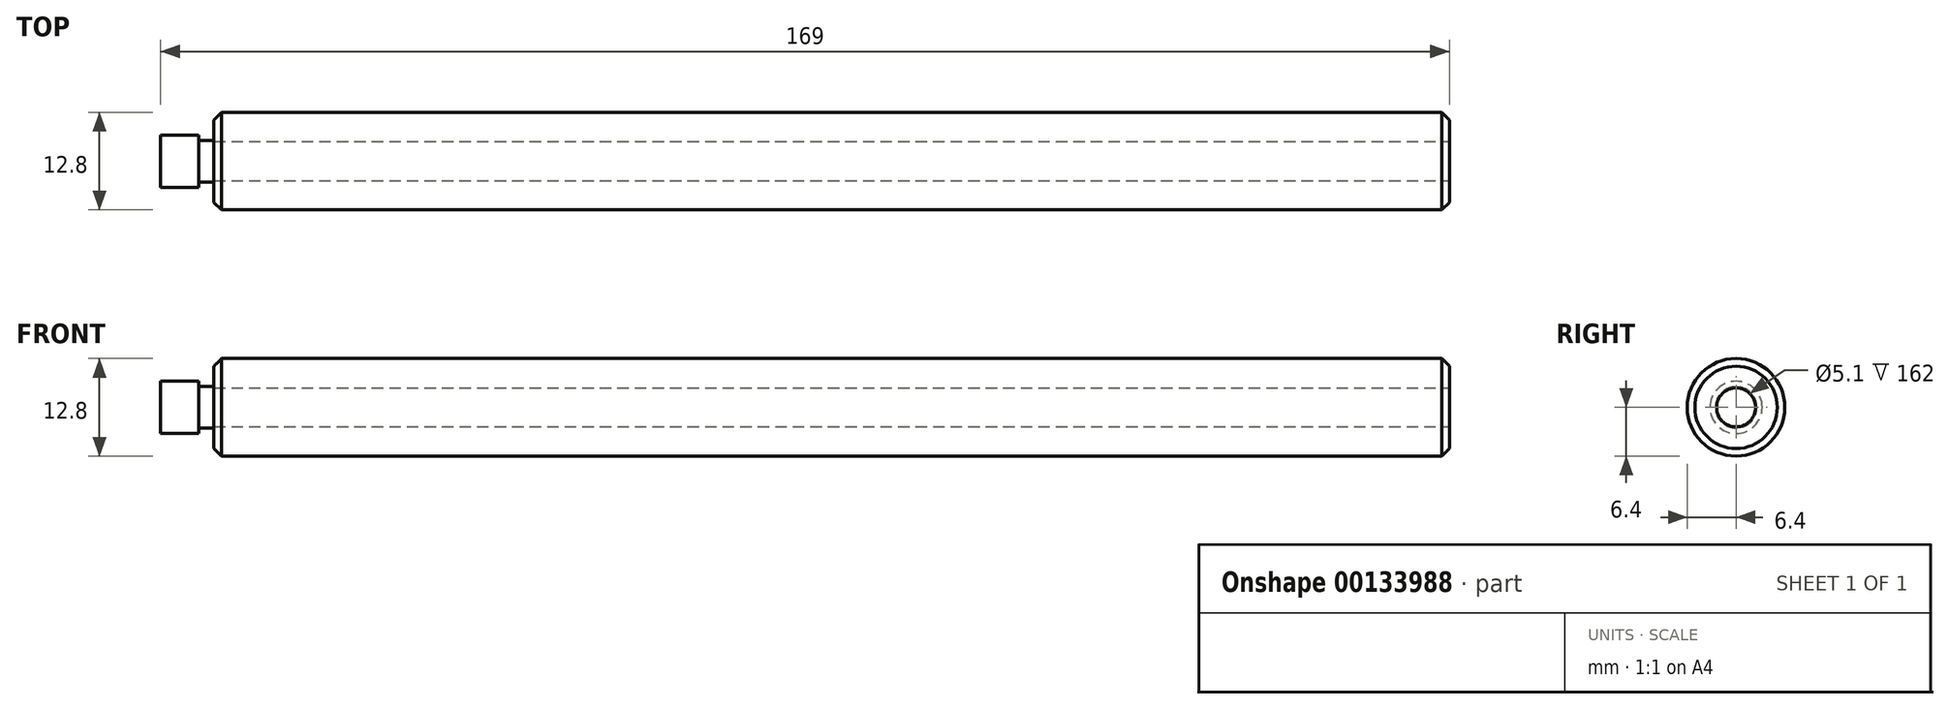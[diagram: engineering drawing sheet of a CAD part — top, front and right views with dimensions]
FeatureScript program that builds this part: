
annotation { "Feature Type Name" : "Feature", "Feature Type Description" : "" }
export const myFeature = defineFeature(function(context is Context, id is Id, definition is map)
    precondition{}
    {
        {
            var Q0;
            Q0=qCreatedBy(makeId("Right.planeOp"),FACE);
            var sketch = newSketch(context, id + "F0", { "sketchPlane" : qUnion([Q0])});
            skCircle(sketch, "E0", {"center": v(0, 0) * mm, "radius": 6.4 * mm});
            skSolve(sketch);
        }
        {
            var Q0;
            Q0=qSketchRegion(id+"F0",true);
            extrude(context, id + "F1", {"entities" : qUnion([Q0]), "oppositeDirection" : true, "depth" : 25.5 * mm});
        }
        {
            var Q0;
            Q0=makeQuery(id+"F1.opExtrude","CAP_FACE",FACE,{"disambiguationData":[OSD([sQuery(id+"F0.wireOp",EDGE,"E0")])],"isStart":true});
            var sketch = newSketch(context, id + "F2", { "sketchPlane" : qUnion([Q0])});
            skLineSegment(sketch, "E1", {"start": v(-6.4, 0) * mm, "end": v(0, 0) * mm, "construction": true});
            skPoint(sketch, "E2", {"position": v(0, 0) * mm});
            skSolve(sketch);
        }
        {
            var Q0;
            Q0=sQuery(id+"F2.wireOp",VERTEX,"E2");
            var Q1;
            Q1=makeQuery(id+"F1.opExtrude","SWEPT_BODY",BODY,{"disambiguationData":[OSD([sQuery(id+"F0.wireOp",EDGE,"E0")])]});
            hole(context, id + "F3", {"style" : HoleStyle.SIMPLE, "endStyle" : HoleEndStyle.THROUGH, "holeDiameter" : 5.1 * mm, "locations" : qUnion([Q0]), "scope" : qUnion([Q1]), "isTappedThrough" : true});
        }
        {
            var Q0;
            Q0=makeQuery(id+"F1.opExtrude","CAP_FACE",FACE,{"disambiguationData":[OSD([sQuery(id+"F0.wireOp",EDGE,"E0")])],"isStart":false});
            var sketch = newSketch(context, id + "F4", { "sketchPlane" : qUnion([Q0])});
            skCircle(sketch, "E3", {"center": v(0, 0) * mm, "radius": 6.4 * mm});
            skSolve(sketch);
        }
        {
            var Q0;
            Q0=makeQuery(id+"F4.imprint","IMPRINT",FACE,{"disambiguationData":[TD([[makeQuery(id+"F4.imprint","IMPRINT",EDGE,{"derivedFrom":makeQuery(id+"F3.hole-0.boolean.opBoolean","INTERSECT",EDGE,{"derivedFrom":[makeQuery(id+"F1.opExtrude","CAP_FACE",FACE,{"disambiguationData":[OSD([sQuery(id+"F0.wireOp",EDGE,"E0")])],"isStart":false}),makeQuery(id+"F3.hole-0.opRevolve","SWEPT_FACE",FACE,{"disambiguationData":[OSD([sQuery(id+"F3.hole-0.sketch.wireOp",EDGE,"core_line_2")])]})]})}),1.0]])]});
            var Q1;
            Q1=makeQuery(id+"F4.imprint","IMPRINT",FACE,{"disambiguationData":[TD([[makeQuery(id+"F4.imprint","IMPRINT",EDGE,{"derivedFrom":sQuery(id+"F4.wireOp",EDGE,"E3")}),-1.0]])]});
            extrude(context, id + "F5", {"entities" : qUnion([Q0, Q1]), "operationType" : NewBodyOperationType.ADD, "depth" : 136.5 * mm});
        }
        {
            var Q0;
            Q0=makeQuery(id+"F5.boolean.opBoolean","MERGE",FACE,{"derivedFrom":[makeQuery(id+"F1.opExtrude","SWEPT_FACE",FACE,{"disambiguationData":[OSD([sQuery(id+"F0.wireOp",EDGE,"E0")])]}),makeQuery(id+"F5.opExtrude","SWEPT_FACE",FACE,{"disambiguationData":[OSD([sQuery(id+"F4.wireOp",EDGE,"E3")])]})]});
            chamfer(context, id + "F6", {"entities" : qUnion([Q0]), "chamferType" : ChamferType.OFFSET_ANGLE, "width" : 1 * mm, "oppositeDirection" : false, "angle" : 45 * degree, "tangentPropagation" : true});
        }
        {
            var Q0;
            Q0=makeQuery(id+"F5.opExtrude","CAP_FACE",FACE,{"disambiguationData":[OSD([sQuery(id+"F4.wireOp",EDGE,"E3")])],"isStart":false});
            var sketch = newSketch(context, id + "F7", { "sketchPlane" : qUnion([Q0])});
            skCircle(sketch, "E4", {"center": v(0, 0) * mm, "radius": 2.73 * mm});
            skSolve(sketch);
        }
        {
            var Q0;
            Q0=qSketchRegion(id+"F7",true);
            extrude(context, id + "F8", {"entities" : qUnion([Q0]), "operationType" : NewBodyOperationType.ADD, "depth" : 7 * mm});
        }
        {
            var Q0;
            Q0=makeQuery(id+"F8.opExtrude","CAP_FACE",FACE,{"disambiguationData":[OSD([sQuery(id+"F7.wireOp",EDGE,"E4")])],"isStart":false});
            var sketch = newSketch(context, id + "F9", { "sketchPlane" : qUnion([Q0])});
            skCircle(sketch, "E5", {"center": v(0, 0) * mm, "radius": 3.43 * mm});
            skSolve(sketch);
        }
        {
            var Q0;
            Q0=qSketchRegion(id+"F9",true);
            extrude(context, id + "F10", {"entities" : qUnion([Q0]), "operationType" : NewBodyOperationType.ADD, "oppositeDirection" : true, "depth" : 5 * mm});
        }
    });
